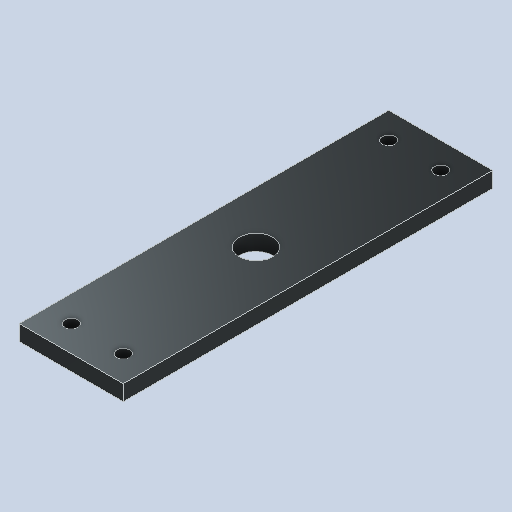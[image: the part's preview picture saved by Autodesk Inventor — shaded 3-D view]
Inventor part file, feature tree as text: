
AUTODESK INVENTOR PART (.ipt)
format: ipt  version: 2023 (Build 270158000, 158)  size: 284,160 bytes
history: native  units: mm
features: hole x3, sketch x2, other x1, extrude x1
ambient origin geometry x8: Origin, YZ Plane, XZ Plane, XY Plane, X Axis, Y Axis, Z Axis, Center Point
bodies: Body1 (feature_tree)
feature tree (7):
  other  "Sólido1"
  extrude  "Extrusão1"  Depth=142.0mm
  hole  "Furo1"  [1 undecoded]
  hole  "Furo2"  [1 undecoded]
  hole  "Furo3"  [1 undecoded]
  sketch  "Esboço1"  dims[d0=40.0mm d1=142.0mm]
  sketch  "Esboço2"  dims[d2=6.0mm d3=0.0mm d4=142.0mm d5=40.0mm d6=20.0mm d7=71.0mm d8=13.0mm d9=6.0mm d10=4.0mm d11=2.0mm d12=90.0deg d13=0.5mm d14=20.594885mm d19=40.0mm d20=10.0mm d21=10.0mm d22=4.5mm d23=4.5mm d24=5.0mm d25=12.0mm d26=8.5mm d27=3.0mm d28=90.0deg d29=0.5mm d30=20.594885mm d32=0.0mm d33=4.5mm d34=0.0mm d35=31.0mm d36=31.0mm d37=31.0mm d38=31.0mm d39=31.0mm d40=31.0mm d41=31.0mm d42=4.5mm d43=0.0mm d44=4.5mm d45=40.0mm d46=10.0mm d47=10.0mm d48=10.0mm d49=10.0mm d50=5.0mm d51=6.0mm d52=3.023mm d53=2.0mm d54=14.3117mm d55=0.5mm d56=20.594885mm d57=10.0mm d58=10.0mm d59=10.0mm]
note: 3 required parameter values undecoded (feature->parameter linkage not recoverable at this tier; creation-order binding heuristic only, values carry confidence <= 0.55)
